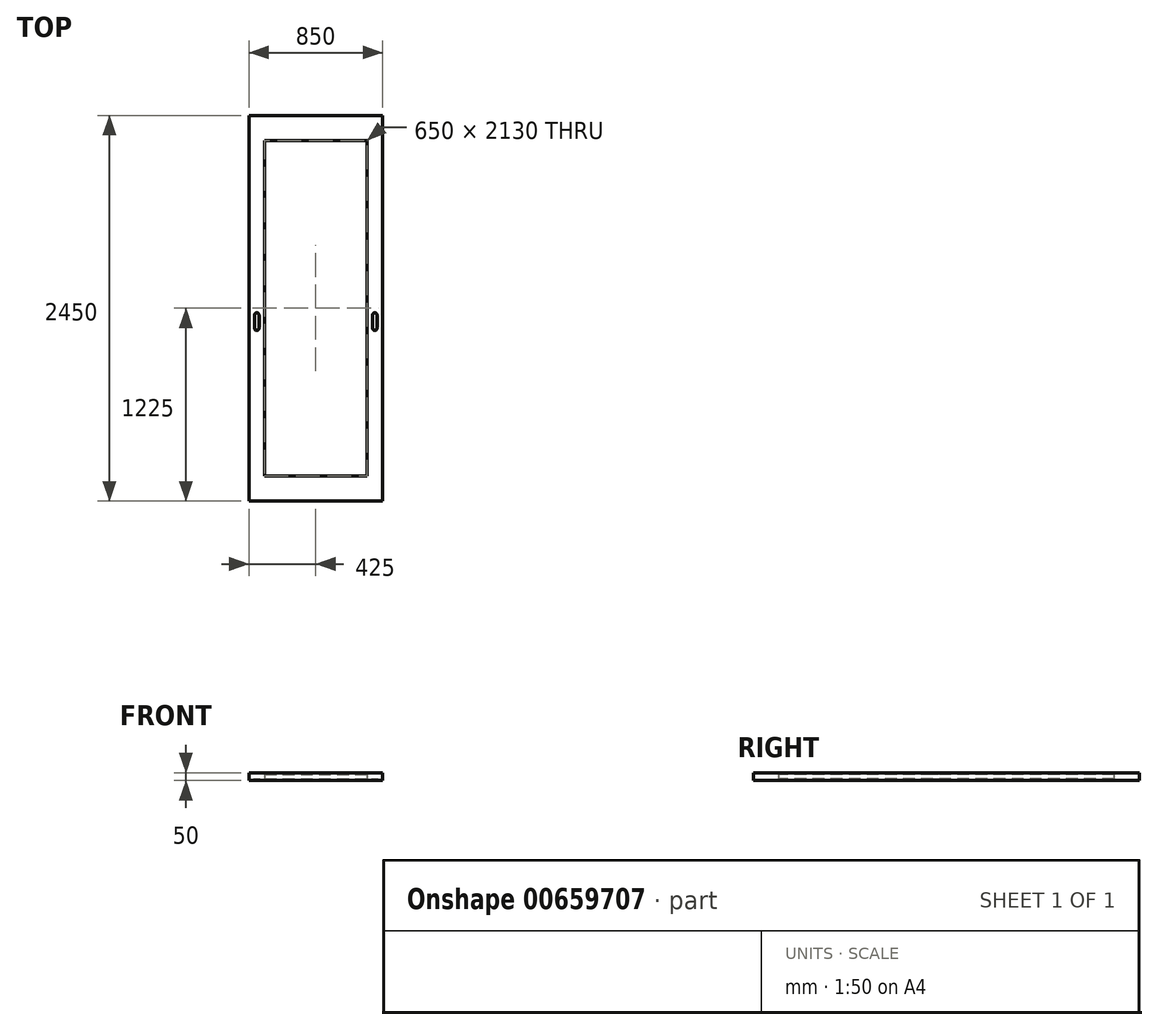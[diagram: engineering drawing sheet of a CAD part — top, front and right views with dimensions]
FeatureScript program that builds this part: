
annotation { "Feature Type Name" : "Feature", "Feature Type Description" : "" }
export const myFeature = defineFeature(function(context is Context, id is Id, definition is map)
    precondition{}
    {
        {
            var Q0;
            Q0=qCreatedBy(makeId("Top.planeOp"),FACE);
            var sketch = newSketch(context, id + "F0", { "sketchPlane" : qUnion([Q0])});
            skLineSegment(sketch, "E0.bottom", {"start": v(0, 0) * mm, "end": v(-850, 0) * mm});
            skLineSegment(sketch, "E0.top", {"start": v(0, 2450) * mm, "end": v(-850, 2450) * mm});
            skLineSegment(sketch, "E0.left", {"start": v(0, 0) * mm, "end": v(0, 2450) * mm});
            skLineSegment(sketch, "E0.right", {"start": v(-850, 0) * mm, "end": v(-850, 2450) * mm});
            skLineSegment(sketch, "E1.bottom", {"start": v(-750, 2290) * mm, "end": v(-100, 2290) * mm});
            skLineSegment(sketch, "E1.top", {"start": v(-750, 160) * mm, "end": v(-100, 160) * mm});
            skLineSegment(sketch, "E1.left", {"start": v(-750, 2290) * mm, "end": v(-750, 160) * mm});
            skLineSegment(sketch, "E1.right", {"start": v(-100, 2290) * mm, "end": v(-100, 160) * mm});
            skSolve(sketch);
        }
        {
            var Q0;
            Q0=makeQuery(id+"F0.imprint","IMPRINT",FACE,{"disambiguationData":[TD([[makeQuery(id+"F0.imprint","IMPRINT",EDGE,{"derivedFrom":sQuery(id+"F0.wireOp",EDGE,"E0.bottom")}),-1.0]])]});
            extrude(context, id + "F1", {"entities" : qUnion([Q0]), "depth" : 50 * mm, "offsetDistance" : 25 * mm});
        }
        {
            var Q0;
            Q0=makeQuery(id+"F1.opExtrude","SWEPT_FACE",FACE,{"disambiguationData":[OSD([sQuery(id+"F0.wireOp",EDGE,"E1.top")])]});
            var sketch = newSketch(context, id + "F2", { "sketchPlane" : qUnion([Q0])});
            skLineSegment(sketch, "E2.0.0", {"start": v(100, 0) * mm, "end": v(750, 0) * mm});
            skLineSegment(sketch, "E2.0.1", {"start": v(750, 0) * mm, "end": v(750, 50) * mm});
            skLineSegment(sketch, "E2.0.2", {"start": v(750, 50) * mm, "end": v(100, 50) * mm});
            skLineSegment(sketch, "E2.0.3", {"start": v(100, 50) * mm, "end": v(100, 0) * mm});
            skLineSegment(sketch, "E3.bottom", {"start": v(750, 40) * mm, "end": v(100, 40) * mm});
            skLineSegment(sketch, "E3.top", {"start": v(750, 10) * mm, "end": v(100, 10) * mm});
            skLineSegment(sketch, "E3.left", {"start": v(750, 40) * mm, "end": v(750, 10) * mm});
            skLineSegment(sketch, "E3.right", {"start": v(100, 40) * mm, "end": v(100, 10) * mm});
            skSolve(sketch);
        }
        {
            var Q0;
            Q0=makeQuery(id+"F2.imprint","IMPRINT",FACE,{"disambiguationData":[TD([[makeQuery(id+"F2.imprint","IMPRINT",EDGE,{"derivedFrom":sQuery(id+"F2.wireOp",EDGE,"E3.bottom")}),1.0]])]});
            extrude(context, id + "F3", {"entities" : qUnion([Q0]), "depth" : 2130 * mm, "offsetDistance" : 25 * mm});
        }
        {
            var Q0;
            Q0=makeQuery(id+"F1.opExtrude","CAP_FACE",FACE,{"disambiguationData":[OSD([sQuery(id+"F0.wireOp",EDGE,"E0.bottom"),sQuery(id+"F0.wireOp",EDGE,"E0.top"),sQuery(id+"F0.wireOp",EDGE,"E0.left"),sQuery(id+"F0.wireOp",EDGE,"E0.right"),sQuery(id+"F0.wireOp",EDGE,"E1.bottom"),sQuery(id+"F0.wireOp",EDGE,"E1.top"),sQuery(id+"F0.wireOp",EDGE,"E1.left"),sQuery(id+"F0.wireOp",EDGE,"E1.right")])],"isStart":false});
            var sketch = newSketch(context, id + "F4", { "sketchPlane" : qUnion([Q0])});
            skLineSegment(sketch, "E4.0", {"start": v(-850, 0) * mm, "end": v(-850, 2450) * mm});
            skLineSegment(sketch, "E5.0", {"start": v(-750, 2290) * mm, "end": v(-750, 160) * mm});
            skLineSegment(sketch, "E6.0", {"start": v(-100, 2290) * mm, "end": v(-100, 160) * mm});
            skLineSegment(sketch, "E7.0", {"start": v(0, 0) * mm, "end": v(0, 2450) * mm});
            skLineSegment(sketch, "E8.left", {"start": v(-815, 1180) * mm, "end": v(-815, 1100) * mm});
            skLineSegment(sketch, "E8.right", {"start": v(-785, 1180) * mm, "end": v(-785, 1100) * mm});
            skLineSegment(sketch, "E9.left", {"start": v(-65, 1100) * mm, "end": v(-65, 1180) * mm});
            skLineSegment(sketch, "E9.right", {"start": v(-35, 1100) * mm, "end": v(-35, 1180) * mm});
            skArc(sketch, "E10", {"start": v(-815, 1180) * mm, "mid": v(-800, 1195) * mm, "end": v(-785, 1180) * mm});
            skArc(sketch, "E11", {"start": v(-815, 1100) * mm, "mid": v(-800, 1085) * mm, "end": v(-785, 1100) * mm});
            skArc(sketch, "E12", {"start": v(-65, 1180) * mm, "mid": v(-50, 1195) * mm, "end": v(-35, 1180) * mm});
            skArc(sketch, "E13", {"start": v(-35, 1100) * mm, "mid": v(-50, 1085) * mm, "end": v(-65, 1100) * mm});
            skSolve(sketch);
        }
        {
            var Q0;
            Q0 = qSketchRegion(id + "F4", true);
            extrude(context, id + "F5", {"entities" : qUnion([Q0]), "operationType" : NewBodyOperationType.REMOVE, "oppositeDirection" : true, "depth" : 7.5 * mm, "offsetDistance" : 25 * mm});
        }
        {
            var Q0;
            Q0=makeQuery(id+"F1.opExtrude","CAP_FACE",FACE,{"disambiguationData":[OSD([sQuery(id+"F0.wireOp",EDGE,"E0.bottom"),sQuery(id+"F0.wireOp",EDGE,"E0.top"),sQuery(id+"F0.wireOp",EDGE,"E0.left"),sQuery(id+"F0.wireOp",EDGE,"E0.right"),sQuery(id+"F0.wireOp",EDGE,"E1.bottom"),sQuery(id+"F0.wireOp",EDGE,"E1.top"),sQuery(id+"F0.wireOp",EDGE,"E1.left"),sQuery(id+"F0.wireOp",EDGE,"E1.right")])],"isStart":true});
            var sketch = newSketch(context, id + "F6", { "sketchPlane" : qUnion([Q0])});
            skLineSegment(sketch, "E14.0", {"start": v(0, 0) * mm, "end": v(0, -2450) * mm});
            skLineSegment(sketch, "E15.0", {"start": v(-100, -2290) * mm, "end": v(-100, -160) * mm});
            skLineSegment(sketch, "E16.0", {"start": v(-750, -2290) * mm, "end": v(-750, -160) * mm});
            skLineSegment(sketch, "E17.0", {"start": v(-850, 0) * mm, "end": v(-850, -2450) * mm});
            skLineSegment(sketch, "E18.0", {"start": v(-750, -160) * mm, "end": v(-100, -160) * mm});
            skLineSegment(sketch, "E19.0", {"start": v(0, 0) * mm, "end": v(-850, 0) * mm});
            skLineSegment(sketch, "E20.left", {"start": v(-30, -1180) * mm, "end": v(-30, -1100) * mm});
            skLineSegment(sketch, "E20.right", {"start": v(-70, -1180) * mm, "end": v(-70, -1100) * mm});
            skLineSegment(sketch, "E21.left", {"start": v(-780, -1180) * mm, "end": v(-780, -1100) * mm});
            skLineSegment(sketch, "E21.right", {"start": v(-820, -1180) * mm, "end": v(-820, -1100) * mm});
            skArc(sketch, "E22", {"start": v(-780, -1100) * mm, "mid": v(-800, -1080) * mm, "end": v(-820, -1100) * mm});
            skArc(sketch, "E23", {"start": v(-780, -1180) * mm, "mid": v(-800, -1200) * mm, "end": v(-820, -1180) * mm});
            skArc(sketch, "E24", {"start": v(-70, -1100) * mm, "mid": v(-50, -1080) * mm, "end": v(-30, -1100) * mm});
            skArc(sketch, "E25", {"start": v(-30, -1180) * mm, "mid": v(-50, -1200) * mm, "end": v(-70, -1180) * mm});
            skSolve(sketch);
        }
        {
            var Q0;
            Q0 = qSketchRegion(id + "F6", true);
            extrude(context, id + "F7", {"entities" : qUnion([Q0]), "operationType" : NewBodyOperationType.REMOVE, "oppositeDirection" : true, "depth" : 7.5 * mm, "offsetDistance" : 25 * mm});
        }
    });
